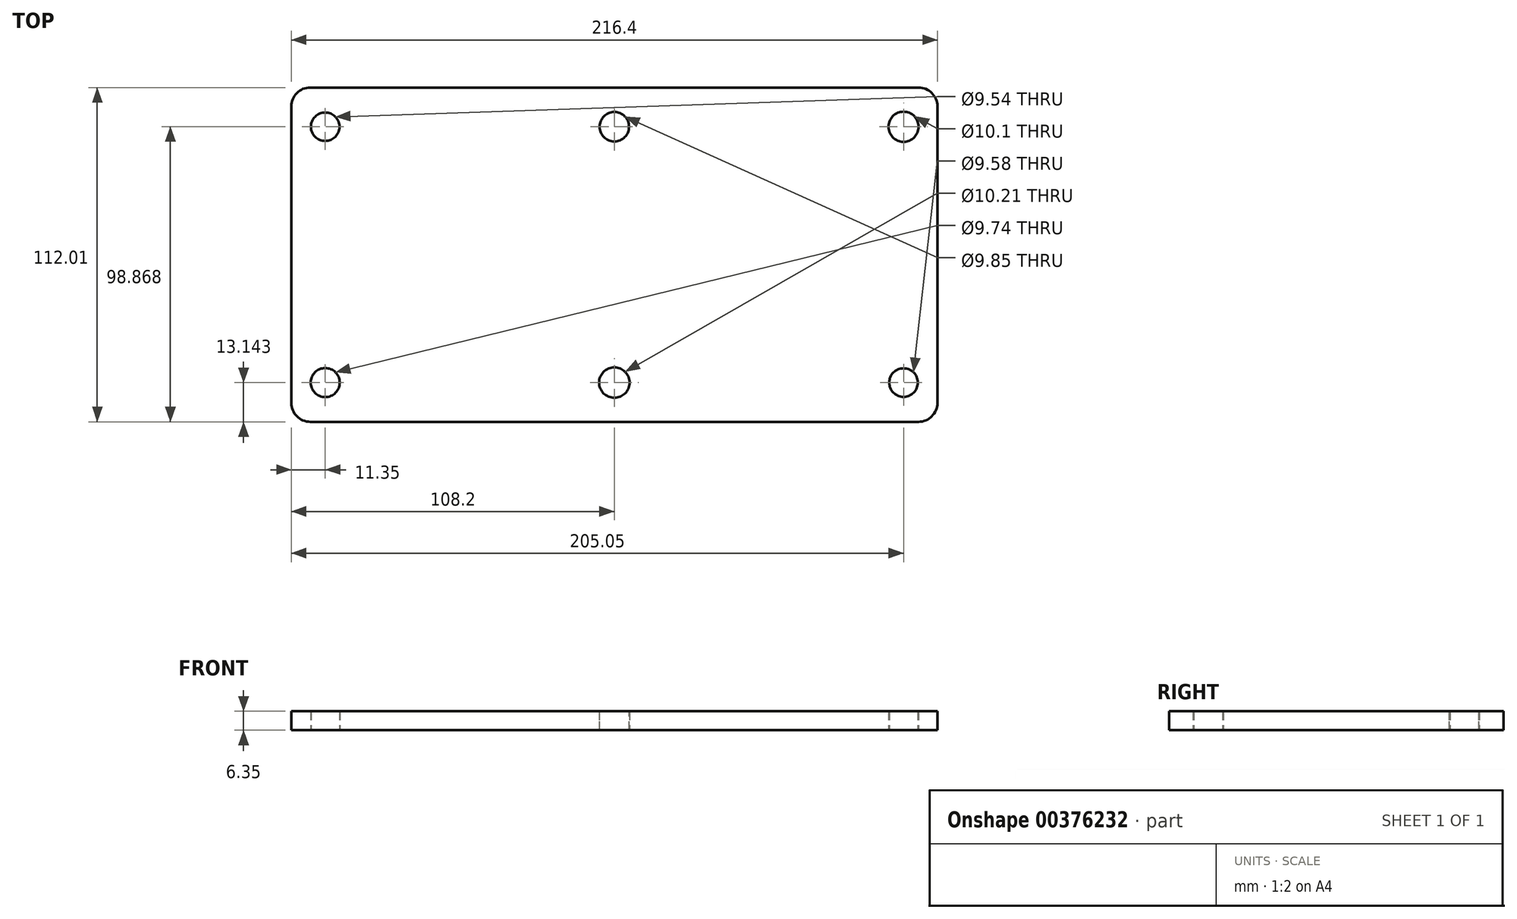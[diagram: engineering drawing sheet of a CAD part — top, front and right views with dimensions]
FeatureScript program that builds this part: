
annotation { "Feature Type Name" : "Feature", "Feature Type Description" : "" }
export const myFeature = defineFeature(function(context is Context, id is Id, definition is map)
    precondition{}
    {
        {
            var Q0;
            Q0=qCreatedBy(makeId("Top.planeOp"),FACE);
            var sketch = newSketch(context, id + "F0", { "sketchPlane" : qUnion([Q0])});
            skLineSegment(sketch, "E0.bottom", {"start": v(-68.88, 51.21) * mm, "end": v(134.82, 51.21) * mm});
            skLineSegment(sketch, "E0.top", {"start": v(-68.88, -60.8) * mm, "end": v(134.82, -60.8) * mm});
            skLineSegment(sketch, "E0.left", {"start": v(-75.23, 44.86) * mm, "end": v(-75.23, -54.45) * mm});
            skLineSegment(sketch, "E0.right", {"start": v(141.17, 44.86) * mm, "end": v(141.17, -54.45) * mm});
            skPoint(sketch, "E1.visualSharp", {"position": v(-75.23, 51.21) * mm});
            skArc(sketch, "E1.filletArc", {"start": v(-68.88, 51.21) * mm, "mid": v(-73.37, 49.35) * mm, "end": v(-75.23, 44.86) * mm});
            skPoint(sketch, "E2.visualSharp", {"position": v(141.17, 51.21) * mm});
            skArc(sketch, "E2.filletArc", {"start": v(141.17, 44.86) * mm, "mid": v(139.31, 49.35) * mm, "end": v(134.82, 51.21) * mm});
            skPoint(sketch, "E3.visualSharp", {"position": v(141.17, -60.8) * mm});
            skArc(sketch, "E3.filletArc", {"start": v(134.82, -60.8) * mm, "mid": v(139.31, -58.94) * mm, "end": v(141.17, -54.45) * mm});
            skPoint(sketch, "E4.visualSharp", {"position": v(-75.23, -60.8) * mm});
            skArc(sketch, "E4.filletArc", {"start": v(-75.23, -54.45) * mm, "mid": v(-73.37, -58.94) * mm, "end": v(-68.88, -60.8) * mm});
            skCircle(sketch, "E5", {"center": v(-63.88, 38.07) * mm, "radius": 4.77 * mm});
            skCircle(sketch, "E6", {"center": v(129.82, 38.07) * mm, "radius": 5.05 * mm});
            skCircle(sketch, "E7", {"center": v(129.82, -47.66) * mm, "radius": 4.79 * mm});
            skCircle(sketch, "E8", {"center": v(32.97, -47.66) * mm, "radius": 5.1 * mm});
            skCircle(sketch, "E9", {"center": v(-63.88, -47.66) * mm, "radius": 4.87 * mm});
            skSolve(sketch);
        }
        {
            var Q0;
            Q0 = qSketchRegion(id + "F0", true);
            extrude(context, id + "F1", {"entities" : qUnion([Q0]), "depth" : 6.35 * mm});
        }
        {
            var Q0;
            Q0=makeQuery(id+"F1.opExtrude","CAP_FACE",FACE,{"disambiguationData":[OSD([sQuery(id+"F0.wireOp",EDGE,"E0.bottom"),sQuery(id+"F0.wireOp",EDGE,"E0.top"),sQuery(id+"F0.wireOp",EDGE,"E0.left"),sQuery(id+"F0.wireOp",EDGE,"E0.right"),sQuery(id+"F0.wireOp",EDGE,"E1.filletArc"),sQuery(id+"F0.wireOp",EDGE,"E2.filletArc"),sQuery(id+"F0.wireOp",EDGE,"E3.filletArc"),sQuery(id+"F0.wireOp",EDGE,"E4.filletArc"),sQuery(id+"F0.wireOp",EDGE,"E5"),sQuery(id+"F0.wireOp",EDGE,"E6"),sQuery(id+"F0.wireOp",EDGE,"E7"),sQuery(id+"F0.wireOp",EDGE,"E8"),sQuery(id+"F0.wireOp",EDGE,"E9")])],"isStart":false});
            var sketch = newSketch(context, id + "F2", { "sketchPlane" : qUnion([Q0])});
            skCircle(sketch, "E10", {"center": v(32.97, 38.07) * mm, "radius": 4.93 * mm});
            skPoint(sketch, "E11.orphan", {"position": v(32.97, -47.66) * mm});
            skPoint(sketch, "E12.orphan", {"position": v(129.82, 38.07) * mm});
            skPoint(sketch, "E13.orphan", {"position": v(-63.88, 38.07) * mm});
            skSolve(sketch);
        }
        {
            var Q0;
            Q0 = qSketchRegion(id + "F2", true);
            extrude(context, id + "F3", {"entities" : qUnion([Q0]), "operationType" : NewBodyOperationType.REMOVE, "oppositeDirection" : true, "depth" : 25.4 * mm});
        }
    });
